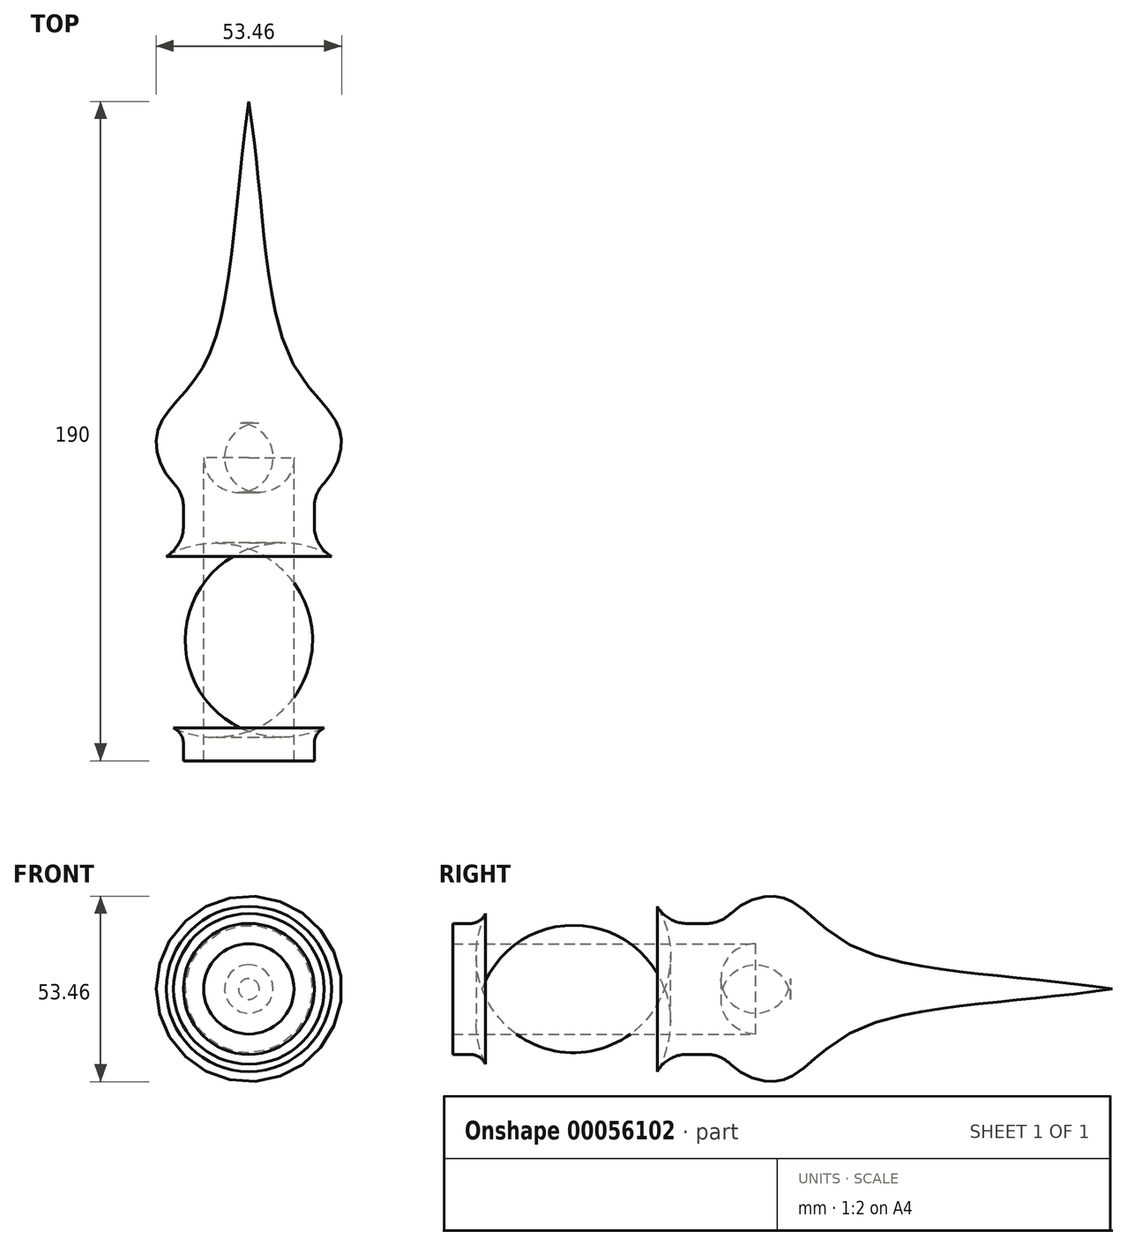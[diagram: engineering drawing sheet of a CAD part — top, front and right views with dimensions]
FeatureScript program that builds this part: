
annotation { "Feature Type Name" : "Feature", "Feature Type Description" : "" }
export const myFeature = defineFeature(function(context is Context, id is Id, definition is map)
    precondition{}
    {
        {
            var Q0;
            Q0=qCreatedBy(makeId("Top.planeOp"),FACE);
            var sketch = newSketch(context, id + "F0", { "sketchPlane" : qUnion([Q0])});
            skLineSegment(sketch, "E0", {"start": v(-13, -9.69) * mm, "end": v(-13, 18.1) * mm});
            skLineSegment(sketch, "E1", {"start": v(-13, 18.1) * mm, "end": v(0, 18.1) * mm});
            skLineSegment(sketch, "E2", {"start": v(0, 18.1) * mm, "end": v(0, 110.8) * mm});
            skLineSegment(sketch, "E3", {"start": v(0, 244.75) * mm, "end": v(0, -222.94) * mm, "construction": true});
            skLineSegment(sketch, "E4", {"start": v(-18.85, -1.19) * mm, "end": v(-18.85, -18) * mm});
            skArc(sketch, "E5", {"start": v(-18.85, -18) * mm, "mid": v(-37.65, -44.45) * mm, "end": v(-18.85, -70.89) * mm});
            skLineSegment(sketch, "E6", {"start": v(-18.85, -70.89) * mm, "end": v(-18.85, -79.2) * mm});
            skLineSegment(sketch, "E7", {"start": v(-18.85, -79.2) * mm, "end": v(-13, -79.2) * mm});
            skLineSegment(sketch, "E8", {"start": v(-13, -79.2) * mm, "end": v(-13, -9.69) * mm});
            skPoint(sketch, "E9", {"position": v(0, 10.9) * mm});
            skFitSpline(sketch, "E10", {"points": [v(-18.85, -1.19) * mm, v(-26.59, 14.53) * mm, v(-13, 34.64) * mm, v(0, 110.8) * mm], "startDerivative": vector(-62.17, 29.02) * mm, "endDerivative": vector(27.46, 186.61) * mm});
            skPoint(sketch, "E11", {"position": v(-13, -44.45) * mm});
            skSolve(sketch);
        }
        {
            var Q0;
            Q0=makeQuery(id+"F0.imprint","IMPRINT",FACE,{"disambiguationData":[TD([[makeQuery(id+"F0.imprint","IMPRINT",EDGE,{"derivedFrom":sQuery(id+"F0.wireOp",EDGE,"E0")}),1.0]])]});
            var Q1;
            Q1=sQuery(id+"F0.wireOp",EDGE,"E3");
            revolve(context, id + "F1", {"entities" : qUnion([Q0]), "axis" : qUnion([Q1]), "revolveType" : RevolveType.FULL});
        }
        {
            var Q0;
            Q0=makeQuery(id+"F1.opRevolve","SWEPT_EDGE",EDGE,{"disambiguationData":[OSD([sQuery(id+"F0.wireOp",EDGE,"E4"),sQuery(id+"F0.wireOp",EDGE,"E10")])]});
            var Q1;
            Q1=makeQuery(id+"F1.opRevolve","SWEPT_EDGE",EDGE,{"disambiguationData":[OSD([sQuery(id+"F0.wireOp",EDGE,"E4"),sQuery(id+"F0.wireOp",EDGE,"E5")])]});
            fillet(context, id + "F2", {"entities" : qUnion([Q0, Q1]), "radius" : 10 * mm, "tangentPropagation" : true, "allowEdgeOverflow" : false});
        }
        {
            var Q0;
            Q0=makeQuery(id+"F1.opRevolve","SWEPT_EDGE",EDGE,{"disambiguationData":[OSD([sQuery(id+"F0.wireOp",EDGE,"E5"),sQuery(id+"F0.wireOp",EDGE,"E6")])]});
            fillet(context, id + "F3", {"entities" : qUnion([Q0]), "radius" : 5 * mm, "tangentPropagation" : true, "allowEdgeOverflow" : false});
        }
        {
            var Q0;
            Q0=makeQuery(id+"F1.opRevolve","SWEPT_EDGE",EDGE,{"disambiguationData":[OSD([sQuery(id+"F0.wireOp",EDGE,"E0"),sQuery(id+"F0.wireOp",EDGE,"E1")])]});
            fillet(context, id + "F4", {"entities" : qUnion([Q0]), "radius" : 10 * mm, "tangentPropagation" : true, "allowEdgeOverflow" : false});
        }
    });
